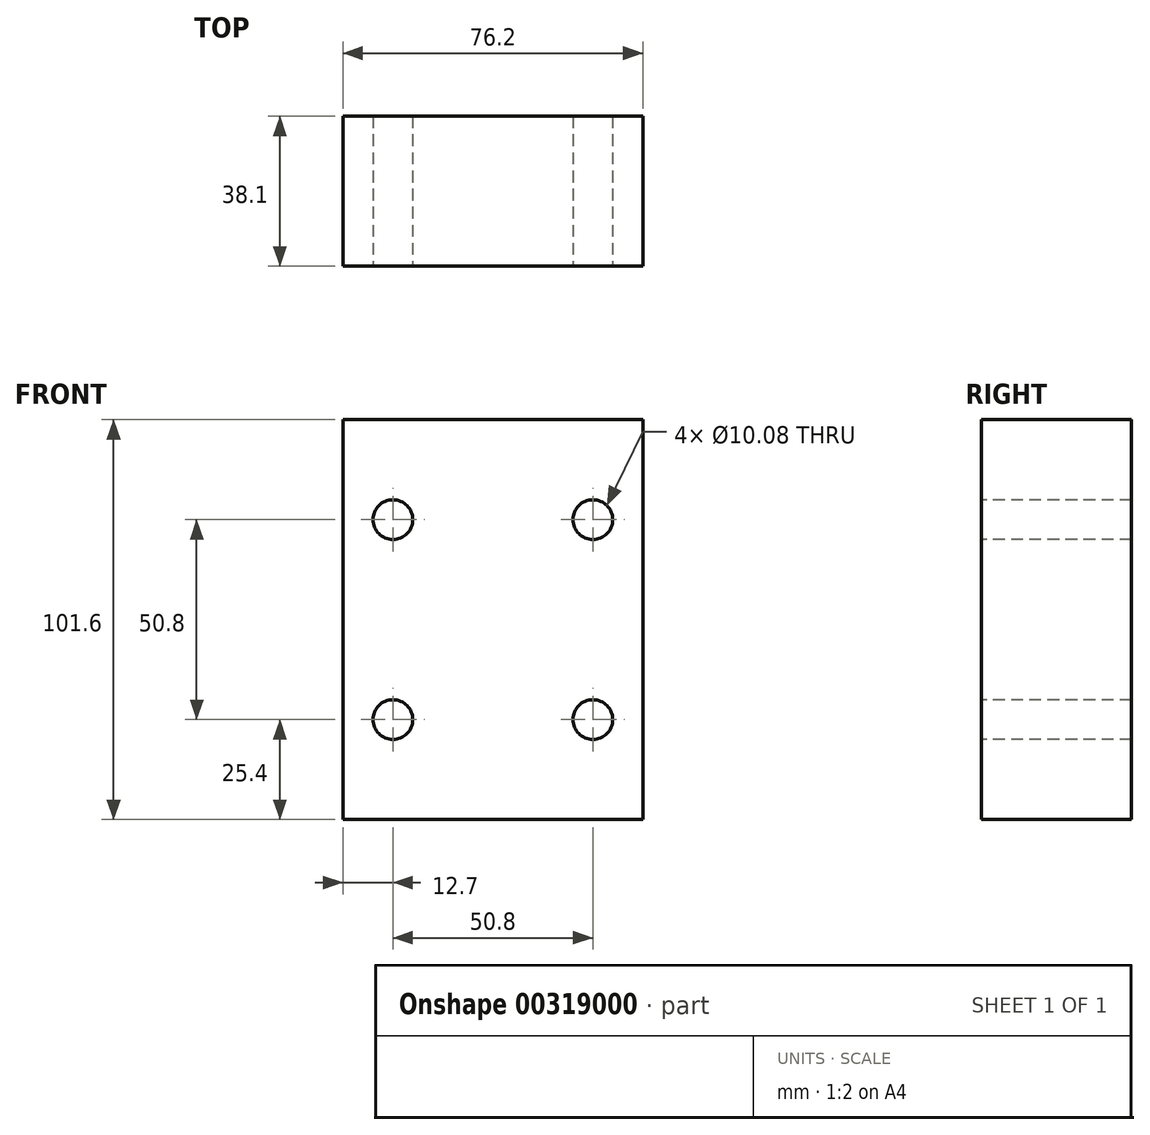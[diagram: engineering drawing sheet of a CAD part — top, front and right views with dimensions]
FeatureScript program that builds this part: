
annotation { "Feature Type Name" : "Feature", "Feature Type Description" : "" }
export const myFeature = defineFeature(function(context is Context, id is Id, definition is map)
    precondition{}
    {
        {
            var Q0;
            Q0=qCreatedBy(makeId("Front.planeOp"),FACE);
            var sketch = newSketch(context, id + "F0", { "sketchPlane" : qUnion([Q0])});
            skLineSegment(sketch, "E0.bottom", {"start": v(38.1, 50.8) * mm, "end": v(-38.1, 50.8) * mm});
            skLineSegment(sketch, "E0.top", {"start": v(38.1, -50.8) * mm, "end": v(-38.1, -50.8) * mm});
            skLineSegment(sketch, "E0.left", {"start": v(38.1, 50.8) * mm, "end": v(38.1, -50.8) * mm});
            skLineSegment(sketch, "E0.right", {"start": v(-38.1, 50.8) * mm, "end": v(-38.1, -50.8) * mm});
            skPoint(sketch, "E0.middle", {"position": v(0, 0) * mm});
            skSolve(sketch);
        }
        {
            var Q0;
            Q0 = qSketchRegion(id + "F0", true);
            extrude(context, id + "F1", {"entities" : qUnion([Q0]), "depth" : 38.1 * mm});
        }
        {
            var Q0;
            Q0=makeQuery(id+"F1.opExtrude","CAP_FACE",FACE,{"disambiguationData":[OSD([sQuery(id+"F0.wireOp",EDGE,"E0.bottom"),sQuery(id+"F0.wireOp",EDGE,"E0.top"),sQuery(id+"F0.wireOp",EDGE,"E0.left"),sQuery(id+"F0.wireOp",EDGE,"E0.right")])],"isStart":false});
            var sketch = newSketch(context, id + "F2", { "sketchPlane" : qUnion([Q0])});
            skPoint(sketch, "E1", {"position": v(-25.4, 25.4) * mm});
            skPoint(sketch, "E2", {"position": v(25.4, 25.4) * mm});
            skPoint(sketch, "E3", {"position": v(25.4, -25.4) * mm});
            skPoint(sketch, "E4", {"position": v(-25.4, -25.4) * mm});
            skSolve(sketch);
        }
        {
            var Q0;
            Q0=sQuery(id+"F2.wireOp",VERTEX,"E1");
            var Q1;
            Q1=sQuery(id+"F2.wireOp",VERTEX,"E2");
            var Q2;
            Q2=sQuery(id+"F2.wireOp",VERTEX,"E4");
            var Q3;
            Q3=sQuery(id+"F2.wireOp",VERTEX,"E3");
            var Q4;
            Q4=makeQuery(id+"F1.opExtrude","SWEPT_BODY",BODY,{"disambiguationData":[OSD([sQuery(id+"F0.wireOp",EDGE,"E0.bottom"),sQuery(id+"F0.wireOp",EDGE,"E0.top"),sQuery(id+"F0.wireOp",EDGE,"E0.left"),sQuery(id+"F0.wireOp",EDGE,"E0.right")])]});
            hole(context, id + "F3", {"style" : HoleStyle.SIMPLE, "endStyle" : HoleEndStyle.THROUGH, "standardTappedOrClearance" : lookupTablePath({ "standard" : "ANSI", "fit" : "Normal (ASME)", "size" : "3/8", "type" : "Clearance" }), "standardBlindInLast" : lookupTablePath({ "fit" : "Free", "standard" : "ANSI", "size" : "3/8", "type" : "Clearance" }), "holeDiameter" : 10.08 * mm, "tappedDepth" : 12.7 * mm, "tapClearance" : 3, "locations" : qUnion([Q0, Q1, Q2, Q3]), "scope" : qUnion([Q4])});
        }
    });
